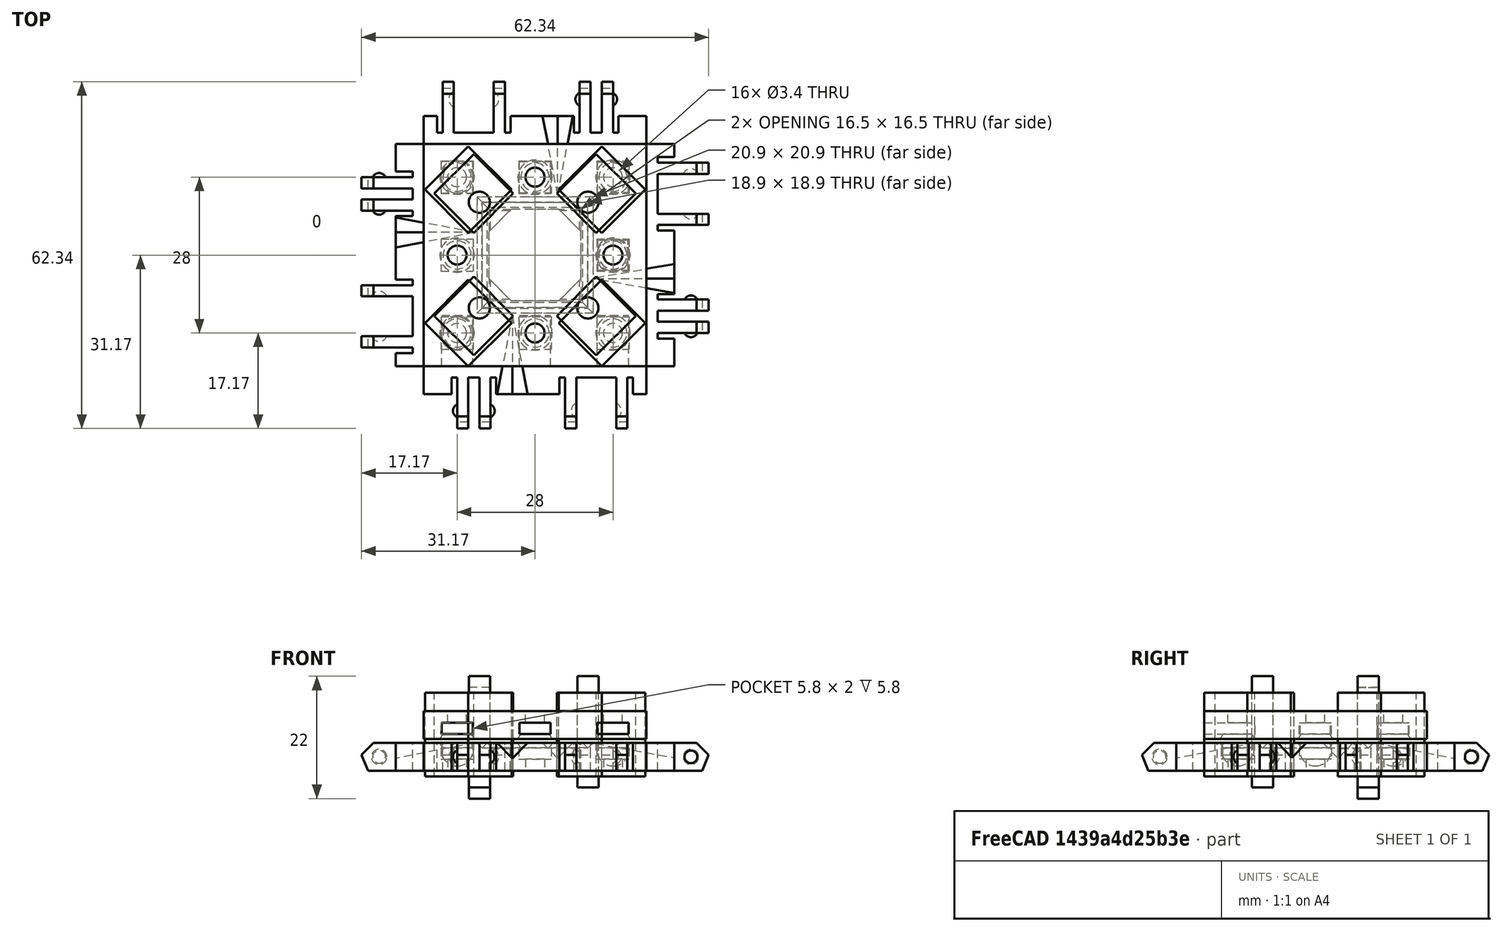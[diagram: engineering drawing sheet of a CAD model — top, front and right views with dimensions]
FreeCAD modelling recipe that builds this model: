
FCSTD DOCUMENT  (FreeCAD 0.17R13522 (Git))
Label: Robot Plates 0.3
License: All rights reserved
LicenseURL: http://en.wikipedia.org/wiki/All_rights_reserved
objects: Part::Box×147, Part::Sphere×51, Part::MultiFuse×48, Part::Cut×47, Part::Cylinder×24, Part::Chamfer×12, Part::Mirroring×2, Part::Fuse×2, App::DocumentObjectGroup×1
note: 333 computed .brp shape members not serialized (recipe doc carries the construction recipe); baked Part::Feature solids carry a one-line shape summary decoded from their .brp

FEATURE [Part::Box] Box  label="Cube"
  AttacherType = Attacher::AttachEngine3D
  Height = 5
  Length = 40
  Placement = pos=(0,0,-2) rot=(0,0,1;0rad)
  Width = 40
FEATURE [Part::Sphere] Sphere003  label="Mag Hole 3"
  Angle1 = -90
  Angle2 = 90
  Angle3 = 360
  AttacherType = Attacher::AttachEngine3D
  Placement = pos=(6,34,1.7) rot=(0,0,1;0rad)
  Radius = 2.85
FEATURE [Part::Sphere] Sphere005  label="Mag Hole 2"
  Angle1 = -90
  Angle2 = 90
  Angle3 = 360
  AttacherType = Attacher::AttachEngine3D
  Placement = pos=(34,20,1.7) rot=(0,0,1;0rad)
  Radius = 2.85
FEATURE [Part::Sphere] Sphere  label="Mag Hole"
  Angle1 = -90
  Angle2 = 90
  Angle3 = 360
  AttacherType = Attacher::AttachEngine3D
  Placement = pos=(6,6,1.7) rot=(0,0,1;0rad)
  Radius = 2.85
FEATURE [Part::MultiFuse] Fusion004
  Shapes = -> [Sphere,Sphere005,Sphere003]
FEATURE [Part::Cut] Cut003
  Base = -> Box
  Tool = -> Fusion004
FEATURE [Part::Box] Box001  label="Cube001"
  AttacherType = Attacher::AttachEngine3D
  Height = 7
  Length = 5
  Width = 40
FEATURE [Part::Box] Box002  label="Cube002"
  AttacherType = Attacher::AttachEngine3D
  Height = 7
  Length = 10
  Placement = pos=(-10,6,0) rot=(0,0,1;0rad)
  Width = 2
FEATURE [Part::Box] Box003  label="Cube003"
  AttacherType = Attacher::AttachEngine3D
  Height = 7
  Length = 10
  Placement = pos=(-10,10,0) rot=(0,0,1;0rad)
  Width = 2
FEATURE [Part::Box] Box004  label="Cube004"
  AttacherType = Attacher::AttachEngine3D
  Height = 7
  Length = 10
  Placement = pos=(-10,25.4,0) rot=(0,0,1;0rad)
  Width = 2
FEATURE [Part::Box] Box005  label="Cube005"
  AttacherType = Attacher::AttachEngine3D
  Height = 7
  Length = 10
  Placement = pos=(-10,34.6,0) rot=(0,0,1;0rad)
  Width = 2
FEATURE [Part::Sphere] Sphere008
  Angle1 = -90
  Angle2 = 90
  Angle3 = 360
  AttacherType = Attacher::AttachEngine3D
  Placement = pos=(-3,6.5,2.5) rot=(0,0,1;0rad)
  Radius = 1.25
FEATURE [Part::Box] Box006  label="Cube006"
  AttacherType = Attacher::AttachEngine3D
  Height = 10
  Length = 13
  Placement = pos=(-10.19,0,-1.19) rot=(0,-1,0;0.785398rad)
  Width = 40
FEATURE [Part::Sphere] Sphere009
  Angle1 = -90
  Angle2 = 90
  Angle3 = 360
  AttacherType = Attacher::AttachEngine3D
  Placement = pos=(-3,11.5,2.5) rot=(0,0,1;0rad)
  Radius = 1.25
FEATURE [Part::Sphere] Sphere010
  Angle1 = -90
  Angle2 = 90
  Angle3 = 360
  AttacherType = Attacher::AttachEngine3D
  Placement = pos=(-3,28,2.5) rot=(0,0,1;0rad)
  Radius = 1.5
FEATURE [Part::Sphere] Sphere011
  Angle1 = -90
  Angle2 = 90
  Angle3 = 360
  AttacherType = Attacher::AttachEngine3D
  Placement = pos=(-3,34,2.5) rot=(0,0,1;0rad)
  Radius = 1.5
FEATURE [Part::MultiFuse] Fusion
  Shapes = -> [Box001,Box002,Box003,Box004,Box005]
FEATURE [Part::Cut] Cut
  Base = -> Fusion
  Tool = -> Box006
FEATURE [Part::MultiFuse] Fusion001
  Shapes = -> [Sphere008,Sphere009,Cut]
FEATURE [Part::MultiFuse] Fusion002
  Shapes = -> [Sphere011,Sphere010]
FEATURE [Part::Cut] Cut001
  Base = -> Fusion001
  Tool = -> Fusion002
FEATURE [Part::Chamfer] Chamfer001
  Base = -> Cut001
  Edges = 4 edges r=4: [Edge31,Edge37,Edge43,Edge46]
FEATURE [Part::Box] Box007  label="Cube007"
  AttacherType = Attacher::AttachEngine3D
  Height = 7
  Length = 4
  Placement = pos=(-1,5,0) rot=(0,0,1;0rad)
  Width = 1
FEATURE [Part::Box] Box008  label="Cube008"
  AttacherType = Attacher::AttachEngine3D
  Height = 7
  Length = 4
  Placement = pos=(-1,8,0) rot=(0,0,1;0rad)
  Width = 2
FEATURE [Part::Box] Box009  label="Cube009"
  AttacherType = Attacher::AttachEngine3D
  Height = 7
  Length = 4
  Placement = pos=(-1,12,0) rot=(0,0,1;0rad)
  Width = 1
FEATURE [Part::Box] Box010  label="Cube010"
  AttacherType = Attacher::AttachEngine3D
  Height = 7
  Length = 4
  Placement = pos=(-1,24.4,0) rot=(0,0,1;0rad)
  Width = 1
FEATURE [Part::Box] Box011  label="Cube011"
  AttacherType = Attacher::AttachEngine3D
  Height = 7
  Length = 4
  Placement = pos=(-1,36.6,0) rot=(0,0,1;0rad)
  Width = 1
FEATURE [Part::Box] Box012  label="Cube012"
  AttacherType = Attacher::AttachEngine3D
  Height = 7
  Length = 4
  Placement = pos=(-1,27.4,0) rot=(0,0,1;0rad)
  Width = 7.2
FEATURE [Part::MultiFuse] Fusion003
  Shapes = -> [Box012,Box009,Box011,Box008,Box010,Box007]
FEATURE [Part::Cut] Cut002
  Base = -> Chamfer001
  Placement = pos=(-5,40,3) rot=(1,0,0;3.14159rad)
  Tool = -> Fusion003
FEATURE [Part::Box] Box013  label="Cube013"
  AttacherType = Attacher::AttachEngine3D
  Height = 10
  Length = 12
  Placement = pos=(-11,-2,-12) rot=(0,0,1;0rad)
  Width = 44
FEATURE [Part::Cut] Cut004
  Base = -> Cut002
  Tool = -> Box013
FEATURE [Part::Box] Box014  label="Cube014"
  AttacherType = Attacher::AttachEngine3D
  Height = 7
  Length = 10
  Placement = pos=(-10,34.6,0) rot=(0,0,1;0rad)
  Width = 2
FEATURE [Part::Box] Box015  label="Cube015"
  AttacherType = Attacher::AttachEngine3D
  Height = 7
  Length = 5
  Width = 40
FEATURE [Part::Box] Box016  label="Cube016"
  AttacherType = Attacher::AttachEngine3D
  Height = 7
  Length = 10
  Placement = pos=(-10,25.4,0) rot=(0,0,1;0rad)
  Width = 2
FEATURE [Part::Box] Box017  label="Cube017"
  AttacherType = Attacher::AttachEngine3D
  Height = 7
  Length = 10
  Placement = pos=(-10,10,0) rot=(0,0,1;0rad)
  Width = 2
FEATURE [Part::Box] Box018  label="Cube018"
  AttacherType = Attacher::AttachEngine3D
  Height = 7
  Length = 10
  Placement = pos=(-10,6,0) rot=(0,0,1;0rad)
  Width = 2
FEATURE [Part::Sphere] Sphere012
  Angle1 = -90
  Angle2 = 90
  Angle3 = 360
  AttacherType = Attacher::AttachEngine3D
  Placement = pos=(-3,6.5,2.5) rot=(0,0,1;0rad)
  Radius = 1.25
FEATURE [Part::Box] Box019  label="Cube019"
  AttacherType = Attacher::AttachEngine3D
  Height = 10
  Length = 13
  Placement = pos=(-10.19,0,-1.19) rot=(0,-1,0;0.785398rad)
  Width = 40
FEATURE [Part::Sphere] Sphere013
  Angle1 = -90
  Angle2 = 90
  Angle3 = 360
  AttacherType = Attacher::AttachEngine3D
  Placement = pos=(-3,11.5,2.5) rot=(0,0,1;0rad)
  Radius = 1.25
FEATURE [Part::Sphere] Sphere014
  Angle1 = -90
  Angle2 = 90
  Angle3 = 360
  AttacherType = Attacher::AttachEngine3D
  Placement = pos=(-3,28,2.5) rot=(0,0,1;0rad)
  Radius = 1.5
FEATURE [Part::Sphere] Sphere015
  Angle1 = -90
  Angle2 = 90
  Angle3 = 360
  AttacherType = Attacher::AttachEngine3D
  Placement = pos=(-3,34,2.5) rot=(0,0,1;0rad)
  Radius = 1.5
FEATURE [Part::MultiFuse] Fusion005
  Shapes = -> [Box015,Box018,Box017,Box016,Box014]
FEATURE [Part::Cut] Cut005
  Base = -> Fusion005
  Tool = -> Box019
FEATURE [Part::MultiFuse] Fusion006
  Shapes = -> [Sphere012,Sphere013,Cut005]
FEATURE [Part::MultiFuse] Fusion007
  Shapes = -> [Sphere015,Sphere014]
FEATURE [Part::Cut] Cut006
  Base = -> Fusion006
  Tool = -> Fusion007
FEATURE [Part::Chamfer] Chamfer002
  Base = -> Cut006
  Edges = 4 edges r=4: [Edge31,Edge37,Edge43,Edge46]
FEATURE [Part::Box] Box020  label="Cube020"
  AttacherType = Attacher::AttachEngine3D
  Height = 7
  Length = 4
  Placement = pos=(-1,5,0) rot=(0,0,1;0rad)
  Width = 1
FEATURE [Part::Box] Box021  label="Cube021"
  AttacherType = Attacher::AttachEngine3D
  Height = 7
  Length = 4
  Placement = pos=(-1,8,0) rot=(0,0,1;0rad)
  Width = 2
FEATURE [Part::Box] Box022  label="Cube022"
  AttacherType = Attacher::AttachEngine3D
  Height = 7
  Length = 4
  Placement = pos=(-1,12,0) rot=(0,0,1;0rad)
  Width = 1
FEATURE [Part::Box] Box023  label="Cube023"
  AttacherType = Attacher::AttachEngine3D
  Height = 7
  Length = 4
  Placement = pos=(-1,24.4,0) rot=(0,0,1;0rad)
  Width = 1
FEATURE [Part::Box] Box024  label="Cube024"
  AttacherType = Attacher::AttachEngine3D
  Height = 7
  Length = 4
  Placement = pos=(-1,36.6,0) rot=(0,0,1;0rad)
  Width = 1
FEATURE [Part::Box] Box025  label="Cube025"
  AttacherType = Attacher::AttachEngine3D
  Height = 7
  Length = 4
  Placement = pos=(-1,27.4,0) rot=(0,0,1;0rad)
  Width = 7.2
FEATURE [Part::MultiFuse] Fusion008
  Shapes = -> [Box025,Box022,Box024,Box021,Box023,Box020]
FEATURE [Part::Cut] Cut007
  Base = -> Chamfer002
  Placement = pos=(-5,40,3) rot=(1,0,0;3.14159rad)
  Tool = -> Fusion008
FEATURE [Part::Box] Box026  label="Cube026"
  AttacherType = Attacher::AttachEngine3D
  Height = 10
  Length = 12
  Placement = pos=(-11,-2,-12) rot=(0,0,1;0rad)
  Width = 44
FEATURE [Part::Cut] Cut008
  Base = -> Cut007
  Placement = pos=(40,0,0) rot=(0,0,1;1.5708rad)
  Tool = -> Box026
FEATURE [Part::Box] Box027  label="Cube027"
  AttacherType = Attacher::AttachEngine3D
  Height = 7
  Length = 4
  Placement = pos=(-1,12,0) rot=(0,0,1;0rad)
  Width = 1
FEATURE [Part::Box] Box028  label="Cube028"
  AttacherType = Attacher::AttachEngine3D
  Height = 10
  Length = 13
  Placement = pos=(-10.19,0,-1.19) rot=(0,-1,0;0.785398rad)
  Width = 40
FEATURE [Part::Box] Box029  label="Cube029"
  AttacherType = Attacher::AttachEngine3D
  Height = 7
  Length = 4
  Placement = pos=(-1,27.4,0) rot=(0,0,1;0rad)
  Width = 7.2
FEATURE [Part::Box] Box030  label="Cube030"
  AttacherType = Attacher::AttachEngine3D
  Height = 7
  Length = 4
  Placement = pos=(-1,5,0) rot=(0,0,1;0rad)
  Width = 1
FEATURE [Part::Box] Box031  label="Cube031"
  AttacherType = Attacher::AttachEngine3D
  Height = 7
  Length = 10
  Placement = pos=(-10,6,0) rot=(0,0,1;0rad)
  Width = 2
FEATURE [Part::Box] Box032  label="Cube032"
  AttacherType = Attacher::AttachEngine3D
  Height = 10
  Length = 12
  Placement = pos=(-11,-2,-12) rot=(0,0,1;0rad)
  Width = 44
FEATURE [Part::Sphere] Sphere016
  Angle1 = -90
  Angle2 = 90
  Angle3 = 360
  AttacherType = Attacher::AttachEngine3D
  Placement = pos=(-3,6.5,2.5) rot=(0,0,1;0rad)
  Radius = 1.25
FEATURE [Part::Box] Box033  label="Cube033"
  AttacherType = Attacher::AttachEngine3D
  Height = 7
  Length = 10
  Placement = pos=(-10,25.4,0) rot=(0,0,1;0rad)
  Width = 2
FEATURE [Part::Box] Box034  label="Cube034"
  AttacherType = Attacher::AttachEngine3D
  Height = 7
  Length = 10
  Placement = pos=(-10,10,0) rot=(0,0,1;0rad)
  Width = 2
FEATURE [Part::Sphere] Sphere017
  Angle1 = -90
  Angle2 = 90
  Angle3 = 360
  AttacherType = Attacher::AttachEngine3D
  Placement = pos=(-3,28,2.5) rot=(0,0,1;0rad)
  Radius = 1.5
FEATURE [Part::Sphere] Sphere018
  Angle1 = -90
  Angle2 = 90
  Angle3 = 360
  AttacherType = Attacher::AttachEngine3D
  Placement = pos=(-3,11.5,2.5) rot=(0,0,1;0rad)
  Radius = 1.25
FEATURE [Part::Box] Box035  label="Cube035"
  AttacherType = Attacher::AttachEngine3D
  Height = 7
  Length = 4
  Placement = pos=(-1,36.6,0) rot=(0,0,1;0rad)
  Width = 1
FEATURE [Part::Sphere] Sphere019
  Angle1 = -90
  Angle2 = 90
  Angle3 = 360
  AttacherType = Attacher::AttachEngine3D
  Placement = pos=(-3,34,2.5) rot=(0,0,1;0rad)
  Radius = 1.5
FEATURE [Part::MultiFuse] Fusion011
  Shapes = -> [Sphere019,Sphere017]
FEATURE [Part::Box] Box036  label="Cube036"
  AttacherType = Attacher::AttachEngine3D
  Height = 7
  Length = 4
  Placement = pos=(-1,8,0) rot=(0,0,1;0rad)
  Width = 2
FEATURE [Part::Box] Box037  label="Cube037"
  AttacherType = Attacher::AttachEngine3D
  Height = 7
  Length = 10
  Placement = pos=(-10,34.6,0) rot=(0,0,1;0rad)
  Width = 2
FEATURE [Part::Box] Box038  label="Cube038"
  AttacherType = Attacher::AttachEngine3D
  Height = 7
  Length = 4
  Placement = pos=(-1,24.4,0) rot=(0,0,1;0rad)
  Width = 1
FEATURE [Part::MultiFuse] Fusion009
  Shapes = -> [Box029,Box027,Box035,Box036,Box038,Box030]
FEATURE [Part::Box] Box039  label="Cube039"
  AttacherType = Attacher::AttachEngine3D
  Height = 7
  Length = 5
  Width = 40
FEATURE [Part::MultiFuse] Fusion012
  Shapes = -> [Box039,Box031,Box034,Box033,Box037]
FEATURE [Part::Cut] Cut011
  Base = -> Fusion012
  Tool = -> Box028
FEATURE [Part::MultiFuse] Fusion010
  Shapes = -> [Sphere016,Sphere018,Cut011]
FEATURE [Part::Cut] Cut012
  Base = -> Fusion010
  Tool = -> Fusion011
FEATURE [Part::Chamfer] Chamfer003
  Base = -> Cut012
  Edges = 4 edges r=4: [Edge31,Edge37,Edge43,Edge46]
FEATURE [Part::Cut] Cut010
  Base = -> Chamfer003
  Placement = pos=(-5,40,3) rot=(1,0,0;3.14159rad)
  Tool = -> Fusion009
FEATURE [Part::Cut] Cut009
  Base = -> Cut010
  Placement = pos=(40,40,0) rot=(0,0,1;3.14159rad)
  Tool = -> Box032
FEATURE [Part::Sphere] Sphere020
  Angle1 = -90
  Angle2 = 90
  Angle3 = 360
  AttacherType = Attacher::AttachEngine3D
  Placement = pos=(-3,11.5,2.5) rot=(0,0,1;0rad)
  Radius = 1.25
FEATURE [Part::Box] Box040  label="Cube040"
  AttacherType = Attacher::AttachEngine3D
  Height = 7
  Length = 10
  Placement = pos=(-10,6,0) rot=(0,0,1;0rad)
  Width = 2
FEATURE [Part::Box] Box041  label="Cube041"
  AttacherType = Attacher::AttachEngine3D
  Height = 7
  Length = 4
  Placement = pos=(-1,8,0) rot=(0,0,1;0rad)
  Width = 2
FEATURE [Part::Box] Box042  label="Cube042"
  AttacherType = Attacher::AttachEngine3D
  Height = 7
  Length = 10
  Placement = pos=(-10,10,0) rot=(0,0,1;0rad)
  Width = 2
FEATURE [Part::Box] Box043  label="Cube043"
  AttacherType = Attacher::AttachEngine3D
  Height = 10
  Length = 12
  Placement = pos=(-11,-2,-12) rot=(0,0,1;0rad)
  Width = 44
FEATURE [Part::Box] Box044  label="Cube044"
  AttacherType = Attacher::AttachEngine3D
  Height = 7
  Length = 4
  Placement = pos=(-1,5,0) rot=(0,0,1;0rad)
  Width = 1
FEATURE [Part::Sphere] Sphere021
  Angle1 = -90
  Angle2 = 90
  Angle3 = 360
  AttacherType = Attacher::AttachEngine3D
  Placement = pos=(-3,28,2.5) rot=(0,0,1;0rad)
  Radius = 1.5
FEATURE [Part::Sphere] Sphere022
  Angle1 = -90
  Angle2 = 90
  Angle3 = 360
  AttacherType = Attacher::AttachEngine3D
  Placement = pos=(-3,6.5,2.5) rot=(0,0,1;0rad)
  Radius = 1.25
FEATURE [Part::Sphere] Sphere023
  Angle1 = -90
  Angle2 = 90
  Angle3 = 360
  AttacherType = Attacher::AttachEngine3D
  Placement = pos=(-3,34,2.5) rot=(0,0,1;0rad)
  Radius = 1.5
FEATURE [Part::Box] Box045  label="Cube045"
  AttacherType = Attacher::AttachEngine3D
  Height = 7
  Length = 4
  Placement = pos=(-1,12,0) rot=(0,0,1;0rad)
  Width = 1
FEATURE [Part::Box] Box046  label="Cube046"
  AttacherType = Attacher::AttachEngine3D
  Height = 7
  Length = 5
  Width = 40
FEATURE [Part::Box] Box047  label="Cube047"
  AttacherType = Attacher::AttachEngine3D
  Height = 7
  Length = 4
  Placement = pos=(-1,36.6,0) rot=(0,0,1;0rad)
  Width = 1
FEATURE [Part::Box] Box048  label="Cube048"
  AttacherType = Attacher::AttachEngine3D
  Height = 7
  Length = 4
  Placement = pos=(-1,24.4,0) rot=(0,0,1;0rad)
  Width = 1
FEATURE [Part::Box] Box049  label="Cube049"
  AttacherType = Attacher::AttachEngine3D
  Height = 7
  Length = 10
  Placement = pos=(-10,25.4,0) rot=(0,0,1;0rad)
  Width = 2
FEATURE [Part::Box] Box050  label="Cube050"
  AttacherType = Attacher::AttachEngine3D
  Height = 10
  Length = 13
  Placement = pos=(-10.19,0,-1.19) rot=(0,-1,0;0.785398rad)
  Width = 40
FEATURE [Part::Box] Box051  label="Cube051"
  AttacherType = Attacher::AttachEngine3D
  Height = 7
  Length = 10
  Placement = pos=(-10,34.6,0) rot=(0,0,1;0rad)
  Width = 2
FEATURE [Part::MultiFuse] Fusion015
  Shapes = -> [Box046,Box040,Box042,Box049,Box051]
FEATURE [Part::Cut] Cut013
  Base = -> Fusion015
  Tool = -> Box050
FEATURE [Part::MultiFuse] Fusion013
  Shapes = -> [Sphere022,Sphere020,Cut013]
FEATURE [Part::MultiFuse] Fusion016
  Shapes = -> [Sphere023,Sphere021]
FEATURE [Part::Cut] Cut014
  Base = -> Fusion013
  Tool = -> Fusion016
FEATURE [Part::Chamfer] Chamfer004
  Base = -> Cut014
  Edges = 4 edges r=4: [Edge31,Edge37,Edge43,Edge46]
FEATURE [Part::Box] Box052  label="Cube052"
  AttacherType = Attacher::AttachEngine3D
  Height = 7
  Length = 4
  Placement = pos=(-1,27.4,0) rot=(0,0,1;0rad)
  Width = 7.2
FEATURE [Part::MultiFuse] Fusion014
  Shapes = -> [Box052,Box045,Box047,Box041,Box048,Box044]
FEATURE [Part::Cut] Cut016
  Base = -> Chamfer004
  Placement = pos=(-5,40,3) rot=(1,0,0;3.14159rad)
  Tool = -> Fusion014
FEATURE [Part::Cut] Cut015
  Base = -> Cut016
  Placement = pos=(0,40,0) rot=(0,0,-1;1.5708rad)
  Tool = -> Box043
FEATURE [Part::Box] Box054  label="Cube054"
  AttacherType = Attacher::AttachEngine3D
  Height = 15
  Length = 10
  Placement = pos=(9,2,-3) rot=(0,0,1;0.785398rad)
  Width = 10
FEATURE [Part::Box] Box055  label="Cube055"
  AttacherType = Attacher::AttachEngine3D
  Height = 15
  Length = 10
  Placement = pos=(31,24,-3) rot=(0,0,1;0.785398rad)
  Width = 10
FEATURE [Part::Box] Box056  label="Cube056"
  AttacherType = Attacher::AttachEngine3D
  Height = 15
  Length = 10
  Placement = pos=(31,2,-3) rot=(0,0,1;0.785398rad)
  Width = 10
FEATURE [Part::Box] Box057  label="Cube057"
  AttacherType = Attacher::AttachEngine3D
  Height = 15
  Length = 10
  Placement = pos=(9,24,-3) rot=(0,0,1;0.785398rad)
  Width = 10
FEATURE [Part::MultiFuse] Fusion017
  Shapes = -> [Box054,Box057,Box056,Box055]
FEATURE [Part::Box] Box058  label="Cube058"
  AttacherType = Attacher::AttachEngine3D
  Height = 5
  Length = 40
  Placement = pos=(0,0,3.7) rot=(0,0,1;0rad)
  Width = 40
FEATURE [Part::Box] Box059  label="Square Nut Hole 008"
  AttacherType = Attacher::AttachEngine3D
  Height = 2
  Length = 5.6
  Placement = pos=(17.2,31.2,4.6) rot=(0,0,1;0rad)
  Width = 5.6
FEATURE [Part::Box] Box060  label="Square Nut Hole 009"
  AttacherType = Attacher::AttachEngine3D
  Height = 2
  Length = 5.6
  Placement = pos=(17.2,-0.85,4.6) rot=(0,0,1;0rad)
  Width = 10
FEATURE [Part::Box] Box061  label="Square Nut Hole 010"
  AttacherType = Attacher::AttachEngine3D
  Height = 2
  Length = 5.6
  Placement = pos=(31.2,-0.85,4.6) rot=(0,0,1;0rad)
  Width = 10
FEATURE [Part::Box] Box062  label="Square Nut Hole 011"
  AttacherType = Attacher::AttachEngine3D
  Height = 2
  Length = 5.4
  Placement = pos=(31.3,17.3,4.6) rot=(0,0,1;0rad)
  Width = 5.4
FEATURE [Part::Box] Box063  label="Square Nut Hole 012"
  AttacherType = Attacher::AttachEngine3D
  Height = 2
  Length = 5.7
  Placement = pos=(3.15,31.15,4.6) rot=(0,0,1;0rad)
  Width = 5.7
FEATURE [Part::Box] Box064  label="Square Nut Hole 013"
  AttacherType = Attacher::AttachEngine3D
  Height = 2
  Length = 5.5
  Placement = pos=(31.25,31.25,4.6) rot=(0,0,1;0rad)
  Width = 5.5
FEATURE [Part::Box] Box065  label="Square Nut Hole 014"
  AttacherType = Attacher::AttachEngine3D
  Height = 2
  Length = 5.8
  Placement = pos=(3.1,17.1,4.6) rot=(0,0,1;0rad)
  Width = 5.8
FEATURE [Part::Box] Box066  label="Square Nut Hole 015"
  AttacherType = Attacher::AttachEngine3D
  Height = 2
  Length = 5.6
  Placement = pos=(3.2,-0.85,4.6) rot=(0,0,1;0rad)
  Width = 10
FEATURE [Part::Sphere] Sphere006  label="Nut Clearence1"
  Angle1 = -90
  Angle2 = 90
  Angle3 = 360
  AttacherType = Attacher::AttachEngine3D
  Placement = pos=(6,6,2.4) rot=(0,0,1;0rad)
  Radius = 3.35
FEATURE [Part::Sphere] Sphere024
  Angle1 = -90
  Angle2 = 90
  Angle3 = 360
  AttacherType = Attacher::AttachEngine3D
  Placement = pos=(6,34,2.4) rot=(0,0,1;0rad)
  Radius = 3.35
FEATURE [Part::Sphere] Sphere007
  Angle1 = -90
  Angle2 = 90
  Angle3 = 360
  AttacherType = Attacher::AttachEngine3D
  Placement = pos=(34,20,2.4) rot=(0,0,1;0rad)
  Radius = 3.35
FEATURE [Part::Sphere] Sphere001
  Angle1 = -90
  Angle2 = 90
  Angle3 = 360
  AttacherType = Attacher::AttachEngine3D
  Placement = pos=(34,6,2.4) rot=(0,0,1;0rad)
  Radius = 3.35
FEATURE [Part::Sphere] Sphere025
  Angle1 = -90
  Angle2 = 90
  Angle3 = 360
  AttacherType = Attacher::AttachEngine3D
  Placement = pos=(20,6,2.4) rot=(0,0,1;0rad)
  Radius = 3.35
FEATURE [Part::Sphere] Sphere026
  Angle1 = -90
  Angle2 = 90
  Angle3 = 360
  AttacherType = Attacher::AttachEngine3D
  Placement = pos=(20,34,2.4) rot=(0,0,1;0rad)
  Radius = 3.35
FEATURE [Part::Sphere] Sphere004
  Angle1 = -90
  Angle2 = 90
  Angle3 = 360
  AttacherType = Attacher::AttachEngine3D
  Placement = pos=(6,20,2.4) rot=(0,0,1;0rad)
  Radius = 3.35
FEATURE [Part::Sphere] Sphere002
  Angle1 = -90
  Angle2 = 90
  Angle3 = 360
  AttacherType = Attacher::AttachEngine3D
  Placement = pos=(34,34,2.4) rot=(0,0,1;0rad)
  Radius = 3.35
FEATURE [Part::Cylinder] Cylinder
  Angle = 360
  AttacherType = Attacher::AttachEngine3D
  Height = 10
  Placement = pos=(6,6,0) rot=(0,0,1;0rad)
  Radius = 1.7
FEATURE [Part::Cylinder] Cylinder002
  Angle = 360
  AttacherType = Attacher::AttachEngine3D
  Height = 10
  Placement = pos=(34,6,0) rot=(0,0,1;0rad)
  Radius = 1.7
FEATURE [Part::Cylinder] Cylinder001
  Angle = 360
  AttacherType = Attacher::AttachEngine3D
  Height = 10
  Placement = pos=(20,6,0) rot=(0,0,1;0rad)
  Radius = 1.7
FEATURE [Part::Cylinder] Cylinder003
  Angle = 360
  AttacherType = Attacher::AttachEngine3D
  Height = 10
  Placement = pos=(34,34,0) rot=(0,0,1;0rad)
  Radius = 1.7
FEATURE [Part::Cylinder] Cylinder004
  Angle = 360
  AttacherType = Attacher::AttachEngine3D
  Height = 10
  Placement = pos=(20,34,0) rot=(0,0,1;0rad)
  Radius = 1.7
FEATURE [Part::Cylinder] Cylinder005
  Angle = 360
  AttacherType = Attacher::AttachEngine3D
  Height = 10
  Placement = pos=(6,34,0) rot=(0,0,1;0rad)
  Radius = 1.7
FEATURE [Part::Cylinder] Cylinder006
  Angle = 360
  AttacherType = Attacher::AttachEngine3D
  Height = 10
  Placement = pos=(6,20,0) rot=(0,0,1;0rad)
  Radius = 1.7
FEATURE [Part::Cylinder] Cylinder007
  Angle = 360
  AttacherType = Attacher::AttachEngine3D
  Height = 10
  Placement = pos=(34,20,0) rot=(0,0,1;0rad)
  Radius = 1.7
FEATURE [Part::MultiFuse] Fusion018
  Shapes = -> [Cylinder,Cylinder004,Cylinder007,Cylinder005,Cylinder006,Cylinder001,Cylinder002,Cylinder003]
FEATURE [Part::MultiFuse] Fusion019
  Shapes = -> [Sphere007,Sphere024,Sphere006,Sphere025,Sphere001,Sphere026,Sphere004,Sphere002]
FEATURE [Part::MultiFuse] Fusion020
  Shapes = -> [Box061,Box065,Box062,Box063,Box064,Box066,Box059,Box060]
FEATURE [Part::Cut] Cut017
  Base = -> Box058
  Tool = -> Fusion020
FEATURE [Part::Cut] Cut019
  Base = -> Cut017
  Tool = -> Fusion019
FEATURE [Part::Cut] Cut018
  Base = -> Cut019
  Tool = -> Fusion018
FEATURE [Part::Cylinder] Cylinder008
  Angle = 360
  AttacherType = Attacher::AttachEngine3D
  Height = 20
  Placement = pos=(10,10.5,-5) rot=(0,0,1;0rad)
  Radius = 1.9
FEATURE [Part::Cylinder] Cylinder009
  Angle = 360
  AttacherType = Attacher::AttachEngine3D
  Height = 20
  Placement = pos=(29.5,10.5,-5) rot=(0,0,1;0rad)
  Radius = 1.9
FEATURE [Part::Cylinder] Cylinder010
  Angle = 360
  AttacherType = Attacher::AttachEngine3D
  Height = 20
  Placement = pos=(29.5,29.5,-5) rot=(0,0,1;0rad)
  Radius = 1.9
FEATURE [Part::Cylinder] Cylinder011
  Angle = 360
  AttacherType = Attacher::AttachEngine3D
  Height = 20
  Placement = pos=(10,29.5,-7) rot=(0,0,1;0rad)
  Radius = 1.9
FEATURE [Part::MultiFuse] Fusion021  label="M2 Screw holes"
  Shapes = -> [Cylinder008,Cylinder009,Cylinder011,Cylinder010]
FEATURE [Part::Box] Box067  label="Square Nut Hole 016"
  AttacherType = Attacher::AttachEngine3D
  Height = 2
  Length = 5.8
  Placement = pos=(31.1,17.1,4.6) rot=(0,0,1;0rad)
  Width = 5.8
FEATURE [Part::Box] Box068  label="Square Nut Hole 017"
  AttacherType = Attacher::AttachEngine3D
  Height = 2
  Length = 5.8
  Placement = pos=(17.1,3.1,4.6) rot=(0,0,1;0rad)
  Width = 5.8
FEATURE [Part::Box] Box069  label="Square Nut Hole 018"
  AttacherType = Attacher::AttachEngine3D
  Height = 2
  Length = 5.8
  Placement = pos=(31.1,3.1,4.6) rot=(0,0,1;0rad)
  Width = 5.8
FEATURE [Part::Box] Box070  label="Square Nut Hole 019"
  AttacherType = Attacher::AttachEngine3D
  Height = 2
  Length = 5.8
  Placement = pos=(3.1,3.1,4.6) rot=(0,0,1;0rad)
  Width = 5.8
FEATURE [Part::Box] Box071  label="Square Nut Hole 020"
  AttacherType = Attacher::AttachEngine3D
  Height = 2
  Length = 5.8
  Placement = pos=(3.1,31.1,4.6) rot=(0,0,1;0rad)
  Width = 5.8
FEATURE [Part::Box] Box072  label="Square Nut Hole 021"
  AttacherType = Attacher::AttachEngine3D
  Height = 2
  Length = 5.8
  Placement = pos=(17.1,31.1,4.6) rot=(0,0,1;0rad)
  Width = 5.8
FEATURE [Part::Box] Box073  label="Square Nut Hole 022"
  AttacherType = Attacher::AttachEngine3D
  Height = 2
  Length = 5.8
  Placement = pos=(31.1,31.1,4.6) rot=(0,0,1;0rad)
  Width = 5.8
FEATURE [Part::Box] Box074  label="Square Nut Hole 023"
  AttacherType = Attacher::AttachEngine3D
  Height = 2
  Length = 5.8
  Placement = pos=(3.1,17.1,4.6) rot=(0,0,1;0rad)
  Width = 5.8
FEATURE [Part::Cylinder] Cylinder012
  Angle = 360
  AttacherType = Attacher::AttachEngine3D
  Height = 10
  Placement = pos=(6,6,0) rot=(0,0,1;0rad)
  Radius = 1.7
FEATURE [Part::Cylinder] Cylinder013
  Angle = 360
  AttacherType = Attacher::AttachEngine3D
  Height = 10
  Placement = pos=(34,34,0) rot=(0,0,1;0rad)
  Radius = 1.7
FEATURE [Part::Cylinder] Cylinder014
  Angle = 360
  AttacherType = Attacher::AttachEngine3D
  Height = 10
  Placement = pos=(20,34,0) rot=(0,0,1;0rad)
  Radius = 1.7
FEATURE [Part::Cylinder] Cylinder015
  Angle = 360
  AttacherType = Attacher::AttachEngine3D
  Height = 10
  Placement = pos=(6,34,0) rot=(0,0,1;0rad)
  Radius = 1.7
FEATURE [Part::Cylinder] Cylinder016
  Angle = 360
  AttacherType = Attacher::AttachEngine3D
  Height = 10
  Placement = pos=(6,20,0) rot=(0,0,1;0rad)
  Radius = 1.7
FEATURE [Part::Cylinder] Cylinder017
  Angle = 360
  AttacherType = Attacher::AttachEngine3D
  Height = 10
  Placement = pos=(34,20,0) rot=(0,0,1;0rad)
  Radius = 1.7
FEATURE [Part::Cylinder] Cylinder018
  Angle = 360
  AttacherType = Attacher::AttachEngine3D
  Height = 10
  Placement = pos=(34,6,0) rot=(0,0,1;0rad)
  Radius = 1.7
FEATURE [Part::Cylinder] Cylinder019
  Angle = 360
  AttacherType = Attacher::AttachEngine3D
  Height = 10
  Placement = pos=(20,6,0) rot=(0,0,1;0rad)
  Radius = 1.7
FEATURE [Part::Box] Box075  label="Cube059"
  AttacherType = Attacher::AttachEngine3D
  Height = 5
  Length = 40
  Placement = pos=(0,0,-2) rot=(0,0,1;0rad)
  Width = 40
FEATURE [Part::Sphere] Sphere027
  Angle1 = -90
  Angle2 = 90
  Angle3 = 360
  AttacherType = Attacher::AttachEngine3D
  Placement = pos=(34,20,2.4) rot=(0,0,1;0rad)
  Radius = 3.35
FEATURE [Part::Sphere] Sphere028  label="Nut Clearence002"
  Angle1 = -90
  Angle2 = 90
  Angle3 = 360
  AttacherType = Attacher::AttachEngine3D
  Placement = pos=(6,6,2.4) rot=(0,0,1;0rad)
  Radius = 3.35
FEATURE [Part::Sphere] Sphere029
  Angle1 = -90
  Angle2 = 90
  Angle3 = 360
  AttacherType = Attacher::AttachEngine3D
  Placement = pos=(34,34,2.4) rot=(0,0,1;0rad)
  Radius = 3.35
FEATURE [Part::Sphere] Sphere030
  Angle1 = -90
  Angle2 = 90
  Angle3 = 360
  AttacherType = Attacher::AttachEngine3D
  Placement = pos=(34,6,2.4) rot=(0,0,1;0rad)
  Radius = 3.35
FEATURE [Part::Sphere] Sphere031
  Angle1 = -90
  Angle2 = 90
  Angle3 = 360
  AttacherType = Attacher::AttachEngine3D
  Placement = pos=(20,6,2.4) rot=(0,0,1;0rad)
  Radius = 3.35
FEATURE [Part::Sphere] Sphere032
  Angle1 = -90
  Angle2 = 90
  Angle3 = 360
  AttacherType = Attacher::AttachEngine3D
  Placement = pos=(6,34,2.4) rot=(0,0,1;0rad)
  Radius = 3.35
FEATURE [Part::Sphere] Sphere033
  Angle1 = -90
  Angle2 = 90
  Angle3 = 360
  AttacherType = Attacher::AttachEngine3D
  Placement = pos=(6,20,2.4) rot=(0,0,1;0rad)
  Radius = 3.35
FEATURE [Part::Sphere] Sphere034
  Angle1 = -90
  Angle2 = 90
  Angle3 = 360
  AttacherType = Attacher::AttachEngine3D
  Placement = pos=(20,34,2.4) rot=(0,0,1;0rad)
  Radius = 3.35
FEATURE [Part::Box] Box076  label="Cube060"
  AttacherType = Attacher::AttachEngine3D
  Height = 15
  Length = 16.5
  Placement = pos=(11.75,11.75,-3) rot=(0,0,1;0rad)
  Width = 16.5
FEATURE [Part::Box] Box077  label="Cube061"
  AttacherType = Attacher::AttachEngine3D
  Height = 15
  Length = 11
  Placement = pos=(8,24,-3) rot=(0,0,1;0.785398rad)
  Width = 11
FEATURE [Part::Box] Box078  label="Cube062"
  AttacherType = Attacher::AttachEngine3D
  Height = 15
  Length = 11
  Placement = pos=(8,0,-3) rot=(0,0,1;0.785398rad)
  Width = 11
FEATURE [Part::Box] Box079  label="Cube063"
  AttacherType = Attacher::AttachEngine3D
  Height = 15
  Length = 11
  Placement = pos=(32,0,-3) rot=(0,0,1;0.785398rad)
  Width = 11
FEATURE [Part::Box] Box080  label="Cube064"
  AttacherType = Attacher::AttachEngine3D
  Height = 15
  Length = 11
  Placement = pos=(32,24,-3) rot=(0,0,1;0.785398rad)
  Width = 11
FEATURE [Part::MultiFuse] Fusion022
  Shapes = -> [Box078,Box077,Box079,Box080]
FEATURE [Part::Cylinder] Cylinder020
  Angle = 360
  AttacherType = Attacher::AttachEngine3D
  Height = 20
  Placement = pos=(29.5,10.5,-5) rot=(0,0,1;0rad)
  Radius = 1.9
FEATURE [Part::Cylinder] Cylinder021
  Angle = 360
  AttacherType = Attacher::AttachEngine3D
  Height = 20
  Placement = pos=(10,29.5,-7) rot=(0,0,1;0rad)
  Radius = 1.9
FEATURE [Part::Cylinder] Cylinder022
  Angle = 360
  AttacherType = Attacher::AttachEngine3D
  Height = 20
  Placement = pos=(10,10.5,-5) rot=(0,0,1;0rad)
  Radius = 1.9
FEATURE [Part::Cylinder] Cylinder023
  Angle = 360
  AttacherType = Attacher::AttachEngine3D
  Height = 20
  Placement = pos=(29.5,29.5,-5) rot=(0,0,1;0rad)
  Radius = 1.9
FEATURE [Part::MultiFuse] Fusion023  label="M2 Screw holes001"
  Shapes = -> [Cylinder022,Cylinder020,Cylinder021,Cylinder023]
FEATURE [Part::MultiFuse] Fusion024  label="Square Nut Hole"
  Shapes = -> [Box067,Box073,Box071,Box069,Box068,Box070,Box072,Box074]
FEATURE [Part::MultiFuse] Fusion025  label="Square Nut Screw Holes"
  Shapes = -> [Cylinder012,Cylinder018,Cylinder016,Cylinder015,Cylinder014,Cylinder013,Cylinder017,Cylinder019]
FEATURE [Part::MultiFuse] Fusion026  label="Nut Chamfers"
  Shapes = -> [Sphere027,Sphere028,Sphere029,Sphere031,Sphere032,Sphere033,Sphere034,Sphere030]
FEATURE [App::DocumentObjectGroup] Group  label="Cubes"
  Group = -> [Fusion017,Fusion022]
FEATURE [Part::Box] Box082  label="Cube066"
  AttacherType = Attacher::AttachEngine3D
  Height = 10
  Length = 15
  Placement = pos=(30.8481,15.8,2.86019) rot=(0.974848,0.205904,-0.085288;0.803573rad)
  Width = 10
FEATURE [Part::Box] Box083  label="Cube067"
  AttacherType = Attacher::AttachEngine3D
  Height = 10
  Length = 21
  Placement = pos=(9.5,9.5,2.1) rot=(0,0,1;0rad)
  Width = 21
FEATURE [Part::Box] Box084  label="Cube068"
  AttacherType = Attacher::AttachEngine3D
  Height = 14
  Length = 17
  Placement = pos=(11.5,11.5,0) rot=(0,0,1;0rad)
  Width = 17
FEATURE [Part::Cut] Cut020
  Base = -> Box083
  Tool = -> Box084
FEATURE [Part::Chamfer] Chamfer007
  Base = -> Cut020
  Edges = 8 edges r=0.95: [Edge4,Edge5,Edge14,Edge16,Edge17,Edge18,Edge19,Edge20]
FEATURE [Part::Chamfer] Chamfer008
  Base = -> Box076
  Edges = 4 edges r=4: [Edge1,Edge3,Edge5,Edge7]
FEATURE [Part::Box] Box085  label="Cube069"
  AttacherType = Attacher::AttachEngine3D
  Height = 15
  Length = 16
  Placement = pos=(12,12,-13) rot=(0,0,1;0rad)
  Width = 16
FEATURE [Part::Box] Box086  label="Cube070"
  AttacherType = Attacher::AttachEngine3D
  Height = 10
  Length = 10
  Placement = pos=(17,32.0919,9.95) rot=(-0.225436,0.969773,-0.093378;0.807337rad)
  Width = 15
FEATURE [Part::Box] Box087  label="Cube071"
  AttacherType = Attacher::AttachEngine3D
  Height = 10
  Length = 10
  Placement = pos=(7.9081,17,9.95) rot=(-0.450607,0.280623,0.847469;1.65638rad)
  Width = 15
FEATURE [Part::Box] Box088  label="Cube072"
  AttacherType = Attacher::AttachEngine3D
  Height = 10
  Length = 10
  Placement = pos=(23,7.9081,9.95) rot=(-0.381178,-0.08861,0.920245;3.06822rad)
  Width = 15
FEATURE [Part::MultiFuse] Fusion027
  Shapes = -> [Box086,Box082,Box087,Box088]
FEATURE [Part::MultiFuse] Fusion028
  Shapes = -> [Cut015,Cut004,Cut008,Cut009]
FEATURE [Part::Box] Box089  label="Cube073"
  AttacherType = Attacher::AttachEngine3D
  Height = 10
  Length = 10
  Placement = pos=(17,32.0919,9.95) rot=(-0.225436,0.969773,-0.093378;0.807337rad)
  Width = 15
FEATURE [Part::Box] Box090  label="Cube074"
  AttacherType = Attacher::AttachEngine3D
  Height = 10
  Length = 15
  Placement = pos=(30.8481,15.8,2.86019) rot=(0.974848,0.205904,-0.085288;0.803573rad)
  Width = 10
FEATURE [Part::Box] Box091  label="Cube075"
  AttacherType = Attacher::AttachEngine3D
  Height = 10
  Length = 10
  Placement = pos=(7.9081,17,9.95) rot=(-0.450607,0.280623,0.847469;1.65638rad)
  Width = 15
FEATURE [Part::Box] Box092  label="Cube076"
  AttacherType = Attacher::AttachEngine3D
  Height = 10
  Length = 10
  Placement = pos=(23,7.9081,9.95) rot=(-0.381178,-0.08861,0.920245;3.06822rad)
  Width = 15
FEATURE [Part::Box] Box093  label="Cube077"
  AttacherType = Attacher::AttachEngine3D
  Height = 7
  Length = 5
  Width = 40
FEATURE [Part::Box] Box094  label="Cube078"
  AttacherType = Attacher::AttachEngine3D
  Height = 7
  Length = 10
  Placement = pos=(-10,6,0) rot=(0,0,1;0rad)
  Width = 2
FEATURE [Part::Box] Box095  label="Cube079"
  AttacherType = Attacher::AttachEngine3D
  Height = 7
  Length = 10
  Placement = pos=(-10,10,0) rot=(0,0,1;0rad)
  Width = 2
FEATURE [Part::Box] Box096  label="Cube080"
  AttacherType = Attacher::AttachEngine3D
  Height = 7
  Length = 10
  Placement = pos=(-10,25.4,0) rot=(0,0,1;0rad)
  Width = 2
FEATURE [Part::Box] Box097  label="Cube081"
  AttacherType = Attacher::AttachEngine3D
  Height = 7
  Length = 10
  Placement = pos=(-10,34.6,0) rot=(0,0,1;0rad)
  Width = 2
FEATURE [Part::Sphere] Sphere035
  Angle1 = -90
  Angle2 = 90
  Angle3 = 360
  AttacherType = Attacher::AttachEngine3D
  Placement = pos=(-3,6.5,2.5) rot=(0,0,1;0rad)
  Radius = 1.25
FEATURE [Part::Box] Box098  label="Cube082"
  AttacherType = Attacher::AttachEngine3D
  Height = 10
  Length = 13
  Placement = pos=(-10.19,0,-1.19) rot=(0,-1,0;0.785398rad)
  Width = 40
FEATURE [Part::Sphere] Sphere036
  Angle1 = -90
  Angle2 = 90
  Angle3 = 360
  AttacherType = Attacher::AttachEngine3D
  Placement = pos=(-3,11.5,2.5) rot=(0,0,1;0rad)
  Radius = 1.25
FEATURE [Part::Sphere] Sphere037
  Angle1 = -90
  Angle2 = 90
  Angle3 = 360
  AttacherType = Attacher::AttachEngine3D
  Placement = pos=(-3,28,2.5) rot=(0,0,1;0rad)
  Radius = 1.5
FEATURE [Part::Sphere] Sphere038
  Angle1 = -90
  Angle2 = 90
  Angle3 = 360
  AttacherType = Attacher::AttachEngine3D
  Placement = pos=(-3,34,2.5) rot=(0,0,1;0rad)
  Radius = 1.5
FEATURE [Part::MultiFuse] Fusion030
  Shapes = -> [Box093,Box094,Box095,Box096,Box097]
FEATURE [Part::Cut] Cut025
  Base = -> Fusion030
  Tool = -> Box098
FEATURE [Part::MultiFuse] Fusion031
  Shapes = -> [Sphere035,Sphere036,Cut025]
FEATURE [Part::MultiFuse] Fusion032
  Shapes = -> [Sphere038,Sphere037]
FEATURE [Part::Cut] Cut026
  Base = -> Fusion031
  Tool = -> Fusion032
FEATURE [Part::Chamfer] Chamfer009
  Base = -> Cut026
  Edges = 4 edges r=4: [Edge31,Edge37,Edge43,Edge46]
FEATURE [Part::Box] Box099  label="Cube083"
  AttacherType = Attacher::AttachEngine3D
  Height = 7
  Length = 4
  Placement = pos=(-1,5,0) rot=(0,0,1;0rad)
  Width = 1
FEATURE [Part::Box] Box100  label="Cube084"
  AttacherType = Attacher::AttachEngine3D
  Height = 7
  Length = 4
  Placement = pos=(-1,8,0) rot=(0,0,1;0rad)
  Width = 2
FEATURE [Part::Box] Box101  label="Cube085"
  AttacherType = Attacher::AttachEngine3D
  Height = 7
  Length = 4
  Placement = pos=(-1,12,0) rot=(0,0,1;0rad)
  Width = 1
FEATURE [Part::Box] Box102  label="Cube086"
  AttacherType = Attacher::AttachEngine3D
  Height = 7
  Length = 4
  Placement = pos=(-1,24.4,0) rot=(0,0,1;0rad)
  Width = 1
FEATURE [Part::Box] Box103  label="Cube087"
  AttacherType = Attacher::AttachEngine3D
  Height = 7
  Length = 4
  Placement = pos=(-1,36.6,0) rot=(0,0,1;0rad)
  Width = 1
FEATURE [Part::Box] Box104  label="Cube088"
  AttacherType = Attacher::AttachEngine3D
  Height = 7
  Length = 4
  Placement = pos=(-1,27.4,0) rot=(0,0,1;0rad)
  Width = 7.2
FEATURE [Part::MultiFuse] Fusion033
  Shapes = -> [Box104,Box101,Box103,Box100,Box102,Box099]
FEATURE [Part::Cut] Cut027
  Base = -> Chamfer009
  Placement = pos=(-5,40,3) rot=(1,0,0;3.14159rad)
  Tool = -> Fusion033
FEATURE [Part::Box] Box105  label="Cube089"
  AttacherType = Attacher::AttachEngine3D
  Height = 10
  Length = 12
  Placement = pos=(-11,-2,-12) rot=(0,0,1;0rad)
  Width = 44
FEATURE [Part::Cut] Cut028
  Base = -> Cut027
  Tool = -> Box105
FEATURE [Part::Box] Box106  label="Cube090"
  AttacherType = Attacher::AttachEngine3D
  Height = 7
  Length = 10
  Placement = pos=(-10,34.6,0) rot=(0,0,1;0rad)
  Width = 2
FEATURE [Part::Box] Box107  label="Cube091"
  AttacherType = Attacher::AttachEngine3D
  Height = 7
  Length = 5
  Width = 40
FEATURE [Part::Box] Box108  label="Cube092"
  AttacherType = Attacher::AttachEngine3D
  Height = 7
  Length = 10
  Placement = pos=(-10,25.4,0) rot=(0,0,1;0rad)
  Width = 2
FEATURE [Part::Box] Box109  label="Cube093"
  AttacherType = Attacher::AttachEngine3D
  Height = 7
  Length = 10
  Placement = pos=(-10,10,0) rot=(0,0,1;0rad)
  Width = 2
FEATURE [Part::Box] Box110  label="Cube094"
  AttacherType = Attacher::AttachEngine3D
  Height = 7
  Length = 10
  Placement = pos=(-10,6,0) rot=(0,0,1;0rad)
  Width = 2
FEATURE [Part::Sphere] Sphere039
  Angle1 = -90
  Angle2 = 90
  Angle3 = 360
  AttacherType = Attacher::AttachEngine3D
  Placement = pos=(-3,6.5,2.5) rot=(0,0,1;0rad)
  Radius = 1.25
FEATURE [Part::Box] Box111  label="Cube095"
  AttacherType = Attacher::AttachEngine3D
  Height = 10
  Length = 13
  Placement = pos=(-10.19,0,-1.19) rot=(0,-1,0;0.785398rad)
  Width = 40
FEATURE [Part::Sphere] Sphere040
  Angle1 = -90
  Angle2 = 90
  Angle3 = 360
  AttacherType = Attacher::AttachEngine3D
  Placement = pos=(-3,11.5,2.5) rot=(0,0,1;0rad)
  Radius = 1.25
FEATURE [Part::Sphere] Sphere041
  Angle1 = -90
  Angle2 = 90
  Angle3 = 360
  AttacherType = Attacher::AttachEngine3D
  Placement = pos=(-3,28,2.5) rot=(0,0,1;0rad)
  Radius = 1.5
FEATURE [Part::Sphere] Sphere042
  Angle1 = -90
  Angle2 = 90
  Angle3 = 360
  AttacherType = Attacher::AttachEngine3D
  Placement = pos=(-3,34,2.5) rot=(0,0,1;0rad)
  Radius = 1.5
FEATURE [Part::MultiFuse] Fusion034
  Shapes = -> [Box107,Box110,Box109,Box108,Box106]
FEATURE [Part::Cut] Cut029
  Base = -> Fusion034
  Tool = -> Box111
FEATURE [Part::MultiFuse] Fusion035
  Shapes = -> [Sphere039,Sphere040,Cut029]
FEATURE [Part::MultiFuse] Fusion036
  Shapes = -> [Sphere042,Sphere041]
FEATURE [Part::Cut] Cut030
  Base = -> Fusion035
  Tool = -> Fusion036
FEATURE [Part::Chamfer] Chamfer010
  Base = -> Cut030
  Edges = 4 edges r=4: [Edge31,Edge37,Edge43,Edge46]
FEATURE [Part::Box] Box112  label="Cube096"
  AttacherType = Attacher::AttachEngine3D
  Height = 7
  Length = 4
  Placement = pos=(-1,5,0) rot=(0,0,1;0rad)
  Width = 1
FEATURE [Part::Box] Box113  label="Cube097"
  AttacherType = Attacher::AttachEngine3D
  Height = 7
  Length = 4
  Placement = pos=(-1,8,0) rot=(0,0,1;0rad)
  Width = 2
FEATURE [Part::Box] Box114  label="Cube098"
  AttacherType = Attacher::AttachEngine3D
  Height = 7
  Length = 4
  Placement = pos=(-1,12,0) rot=(0,0,1;0rad)
  Width = 1
FEATURE [Part::Box] Box115  label="Cube099"
  AttacherType = Attacher::AttachEngine3D
  Height = 7
  Length = 4
  Placement = pos=(-1,24.4,0) rot=(0,0,1;0rad)
  Width = 1
FEATURE [Part::Box] Box116  label="Cube100"
  AttacherType = Attacher::AttachEngine3D
  Height = 7
  Length = 4
  Placement = pos=(-1,36.6,0) rot=(0,0,1;0rad)
  Width = 1
FEATURE [Part::Box] Box117  label="Cube101"
  AttacherType = Attacher::AttachEngine3D
  Height = 7
  Length = 4
  Placement = pos=(-1,27.4,0) rot=(0,0,1;0rad)
  Width = 7.2
FEATURE [Part::MultiFuse] Fusion037
  Shapes = -> [Box117,Box114,Box116,Box113,Box115,Box112]
FEATURE [Part::Cut] Cut031
  Base = -> Chamfer010
  Placement = pos=(-5,40,3) rot=(1,0,0;3.14159rad)
  Tool = -> Fusion037
FEATURE [Part::Box] Box118  label="Cube102"
  AttacherType = Attacher::AttachEngine3D
  Height = 10
  Length = 12
  Placement = pos=(-11,-2,-12) rot=(0,0,1;0rad)
  Width = 44
FEATURE [Part::Cut] Cut032
  Base = -> Cut031
  Placement = pos=(40,0,0) rot=(0,0,1;1.5708rad)
  Tool = -> Box118
FEATURE [Part::Box] Box119  label="Cube103"
  AttacherType = Attacher::AttachEngine3D
  Height = 7
  Length = 4
  Placement = pos=(-1,12,0) rot=(0,0,1;0rad)
  Width = 1
FEATURE [Part::Box] Box120  label="Cube104"
  AttacherType = Attacher::AttachEngine3D
  Height = 10
  Length = 13
  Placement = pos=(-10.19,0,-1.19) rot=(0,-1,0;0.785398rad)
  Width = 40
FEATURE [Part::Box] Box121  label="Cube105"
  AttacherType = Attacher::AttachEngine3D
  Height = 7
  Length = 4
  Placement = pos=(-1,27.4,0) rot=(0,0,1;0rad)
  Width = 7.2
FEATURE [Part::Box] Box122  label="Cube106"
  AttacherType = Attacher::AttachEngine3D
  Height = 7
  Length = 4
  Placement = pos=(-1,5,0) rot=(0,0,1;0rad)
  Width = 1
FEATURE [Part::Box] Box123  label="Cube107"
  AttacherType = Attacher::AttachEngine3D
  Height = 7
  Length = 10
  Placement = pos=(-10,6,0) rot=(0,0,1;0rad)
  Width = 2
FEATURE [Part::Box] Box124  label="Cube108"
  AttacherType = Attacher::AttachEngine3D
  Height = 10
  Length = 12
  Placement = pos=(-11,-2,-12) rot=(0,0,1;0rad)
  Width = 44
FEATURE [Part::Sphere] Sphere043
  Angle1 = -90
  Angle2 = 90
  Angle3 = 360
  AttacherType = Attacher::AttachEngine3D
  Placement = pos=(-3,6.5,2.5) rot=(0,0,1;0rad)
  Radius = 1.25
FEATURE [Part::Box] Box125  label="Cube109"
  AttacherType = Attacher::AttachEngine3D
  Height = 7
  Length = 10
  Placement = pos=(-10,25.4,0) rot=(0,0,1;0rad)
  Width = 2
FEATURE [Part::Box] Box126  label="Cube110"
  AttacherType = Attacher::AttachEngine3D
  Height = 7
  Length = 10
  Placement = pos=(-10,10,0) rot=(0,0,1;0rad)
  Width = 2
FEATURE [Part::Sphere] Sphere044
  Angle1 = -90
  Angle2 = 90
  Angle3 = 360
  AttacherType = Attacher::AttachEngine3D
  Placement = pos=(-3,28,2.5) rot=(0,0,1;0rad)
  Radius = 1.5
FEATURE [Part::Sphere] Sphere045
  Angle1 = -90
  Angle2 = 90
  Angle3 = 360
  AttacherType = Attacher::AttachEngine3D
  Placement = pos=(-3,11.5,2.5) rot=(0,0,1;0rad)
  Radius = 1.25
FEATURE [Part::Box] Box127  label="Cube111"
  AttacherType = Attacher::AttachEngine3D
  Height = 7
  Length = 4
  Placement = pos=(-1,36.6,0) rot=(0,0,1;0rad)
  Width = 1
FEATURE [Part::Sphere] Sphere046
  Angle1 = -90
  Angle2 = 90
  Angle3 = 360
  AttacherType = Attacher::AttachEngine3D
  Placement = pos=(-3,34,2.5) rot=(0,0,1;0rad)
  Radius = 1.5
FEATURE [Part::MultiFuse] Fusion040
  Shapes = -> [Sphere046,Sphere044]
FEATURE [Part::Box] Box128  label="Cube112"
  AttacherType = Attacher::AttachEngine3D
  Height = 7
  Length = 4
  Placement = pos=(-1,8,0) rot=(0,0,1;0rad)
  Width = 2
FEATURE [Part::Box] Box129  label="Cube113"
  AttacherType = Attacher::AttachEngine3D
  Height = 7
  Length = 10
  Placement = pos=(-10,34.6,0) rot=(0,0,1;0rad)
  Width = 2
FEATURE [Part::Box] Box130  label="Cube114"
  AttacherType = Attacher::AttachEngine3D
  Height = 7
  Length = 4
  Placement = pos=(-1,24.4,0) rot=(0,0,1;0rad)
  Width = 1
FEATURE [Part::MultiFuse] Fusion038
  Shapes = -> [Box121,Box119,Box127,Box128,Box130,Box122]
FEATURE [Part::Box] Box131  label="Cube115"
  AttacherType = Attacher::AttachEngine3D
  Height = 7
  Length = 5
  Width = 40
FEATURE [Part::MultiFuse] Fusion041
  Shapes = -> [Box131,Box123,Box126,Box125,Box129]
FEATURE [Part::Cut] Cut035
  Base = -> Fusion041
  Tool = -> Box120
FEATURE [Part::MultiFuse] Fusion039
  Shapes = -> [Sphere043,Sphere045,Cut035]
FEATURE [Part::Cut] Cut036
  Base = -> Fusion039
  Tool = -> Fusion040
FEATURE [Part::Chamfer] Chamfer011
  Base = -> Cut036
  Edges = 4 edges r=4: [Edge31,Edge37,Edge43,Edge46]
FEATURE [Part::Cut] Cut034
  Base = -> Chamfer011
  Placement = pos=(-5,40,3) rot=(1,0,0;3.14159rad)
  Tool = -> Fusion038
FEATURE [Part::Cut] Cut033
  Base = -> Cut034
  Placement = pos=(40,40,0) rot=(0,0,1;3.14159rad)
  Tool = -> Box124
FEATURE [Part::Sphere] Sphere047
  Angle1 = -90
  Angle2 = 90
  Angle3 = 360
  AttacherType = Attacher::AttachEngine3D
  Placement = pos=(-3,11.5,2.5) rot=(0,0,1;0rad)
  Radius = 1.25
FEATURE [Part::Box] Box132  label="Cube116"
  AttacherType = Attacher::AttachEngine3D
  Height = 7
  Length = 10
  Placement = pos=(-10,6,0) rot=(0,0,1;0rad)
  Width = 2
FEATURE [Part::Box] Box133  label="Cube117"
  AttacherType = Attacher::AttachEngine3D
  Height = 7
  Length = 4
  Placement = pos=(-1,8,0) rot=(0,0,1;0rad)
  Width = 2
FEATURE [Part::Box] Box134  label="Cube118"
  AttacherType = Attacher::AttachEngine3D
  Height = 7
  Length = 10
  Placement = pos=(-10,10,0) rot=(0,0,1;0rad)
  Width = 2
FEATURE [Part::Box] Box135  label="Cube119"
  AttacherType = Attacher::AttachEngine3D
  Height = 10
  Length = 12
  Placement = pos=(-11,-2,-12) rot=(0,0,1;0rad)
  Width = 44
FEATURE [Part::Box] Box136  label="Cube120"
  AttacherType = Attacher::AttachEngine3D
  Height = 7
  Length = 4
  Placement = pos=(-1,5,0) rot=(0,0,1;0rad)
  Width = 1
FEATURE [Part::Sphere] Sphere048
  Angle1 = -90
  Angle2 = 90
  Angle3 = 360
  AttacherType = Attacher::AttachEngine3D
  Placement = pos=(-3,28,2.5) rot=(0,0,1;0rad)
  Radius = 1.5
FEATURE [Part::Sphere] Sphere049
  Angle1 = -90
  Angle2 = 90
  Angle3 = 360
  AttacherType = Attacher::AttachEngine3D
  Placement = pos=(-3,6.5,2.5) rot=(0,0,1;0rad)
  Radius = 1.25
FEATURE [Part::Sphere] Sphere050
  Angle1 = -90
  Angle2 = 90
  Angle3 = 360
  AttacherType = Attacher::AttachEngine3D
  Placement = pos=(-3,34,2.5) rot=(0,0,1;0rad)
  Radius = 1.5
FEATURE [Part::Box] Box137  label="Cube121"
  AttacherType = Attacher::AttachEngine3D
  Height = 7
  Length = 4
  Placement = pos=(-1,12,0) rot=(0,0,1;0rad)
  Width = 1
FEATURE [Part::Box] Box138  label="Cube122"
  AttacherType = Attacher::AttachEngine3D
  Height = 7
  Length = 5
  Width = 40
FEATURE [Part::Box] Box139  label="Cube123"
  AttacherType = Attacher::AttachEngine3D
  Height = 7
  Length = 4
  Placement = pos=(-1,36.6,0) rot=(0,0,1;0rad)
  Width = 1
FEATURE [Part::Box] Box140  label="Cube124"
  AttacherType = Attacher::AttachEngine3D
  Height = 7
  Length = 4
  Placement = pos=(-1,24.4,0) rot=(0,0,1;0rad)
  Width = 1
FEATURE [Part::Box] Box141  label="Cube125"
  AttacherType = Attacher::AttachEngine3D
  Height = 7
  Length = 10
  Placement = pos=(-10,25.4,0) rot=(0,0,1;0rad)
  Width = 2
FEATURE [Part::Box] Box142  label="Cube126"
  AttacherType = Attacher::AttachEngine3D
  Height = 10
  Length = 13
  Placement = pos=(-10.19,0,-1.19) rot=(0,-1,0;0.785398rad)
  Width = 40
FEATURE [Part::Box] Box143  label="Cube127"
  AttacherType = Attacher::AttachEngine3D
  Height = 7
  Length = 10
  Placement = pos=(-10,34.6,0) rot=(0,0,1;0rad)
  Width = 2
FEATURE [Part::MultiFuse] Fusion044
  Shapes = -> [Box138,Box132,Box134,Box141,Box143]
FEATURE [Part::Cut] Cut037
  Base = -> Fusion044
  Tool = -> Box142
FEATURE [Part::MultiFuse] Fusion042
  Shapes = -> [Sphere049,Sphere047,Cut037]
FEATURE [Part::MultiFuse] Fusion045
  Shapes = -> [Sphere050,Sphere048]
FEATURE [Part::Cut] Cut038
  Base = -> Fusion042
  Tool = -> Fusion045
FEATURE [Part::Chamfer] Chamfer012
  Base = -> Cut038
  Edges = 4 edges r=4: [Edge31,Edge37,Edge43,Edge46]
FEATURE [Part::Box] Box144  label="Cube128"
  AttacherType = Attacher::AttachEngine3D
  Height = 7
  Length = 4
  Placement = pos=(-1,27.4,0) rot=(0,0,1;0rad)
  Width = 7.2
FEATURE [Part::MultiFuse] Fusion043
  Shapes = -> [Box144,Box137,Box139,Box133,Box140,Box136]
FEATURE [Part::Cut] Cut040
  Base = -> Chamfer012
  Placement = pos=(-5,40,3) rot=(1,0,0;3.14159rad)
  Tool = -> Fusion043
FEATURE [Part::Cut] Cut039
  Base = -> Cut040
  Placement = pos=(0,40,0) rot=(0,0,-1;1.5708rad)
  Tool = -> Box135
FEATURE [Part::MultiFuse] Fusion046
  Shapes = -> [Cut039,Cut028,Cut032,Cut033]
FEATURE [Part::MultiFuse] Fusion047
  Placement = pos=(0,40,6.7) rot=(1,0,0;3.14159rad)
  Shapes = -> [Fusion026,Fusion024,Fusion025]
FEATURE [Part::MultiFuse] Fusion048
  Shapes = -> [Box089,Box091,Box090,Box092]
FEATURE [Part::Box] Box145  label="Cube129"
  AttacherType = Attacher::AttachEngine3D
  Height = 15
  Length = 16
  Placement = pos=(12,12,-13) rot=(0,0,1;0rad)
  Width = 16
FEATURE [Part::Box] Box146  label="Cube130"
  AttacherType = Attacher::AttachEngine3D
  Height = 15
  Length = 16.5
  Placement = pos=(11.75,11.75,-3) rot=(0,0,1;0rad)
  Width = 16.5
FEATURE [Part::Chamfer] Chamfer013
  Base = -> Box146
  Edges = 4 edges r=4: [Edge1,Edge3,Edge5,Edge7]
FEATURE [Part::Box] Box147  label="Cube131"
  AttacherType = Attacher::AttachEngine3D
  Height = 10
  Length = 21
  Placement = pos=(9.5,9.5,2.1) rot=(0,0,1;0rad)
  Width = 21
FEATURE [Part::Box] Box148  label="Cube132"
  AttacherType = Attacher::AttachEngine3D
  Height = 14
  Length = 17
  Placement = pos=(11.5,11.5,0) rot=(0,0,1;0rad)
  Width = 17
FEATURE [Part::Cut] Cut043
  Base = -> Box147
  Tool = -> Box148
FEATURE [Part::Chamfer] Chamfer014
  Base = -> Cut043
  Edges = 8 edges r=0.95: [Edge4,Edge5,Edge14,Edge16,Edge17,Edge18,Edge19,Edge20]
FEATURE [Part::Cut] Cut047
  Base = -> Cut003
  Tool = -> Chamfer007
FEATURE [Part::Cut] Cut048
  Base = -> Cut047
  Tool = -> Chamfer008
FEATURE [Part::Cut] Cut049
  Base = -> Cut048
  Tool = -> Box085
FEATURE [Part::Mirroring] Part__Mirroring  label="Fusion028 (Mirror #1)"
  Base = (0,0,0)
  Normal = (0,0,1)
  Placement = pos=(0,0,1) rot=(0,0,1;0rad)
  Source = -> Fusion028
FEATURE [Part::Fuse] Fusion050
  Base = -> Cut049
  Tool = -> Part__Mirroring
FEATURE [Part::Cut] Cut050
  Base = -> Fusion050
  Tool = -> Fusion027
FEATURE [Part::Mirroring] Part__Mirroring001  label="Fusion046 (Mirror #2)"
  Base = (0,0,0)
  Normal = (0,0,1)
  Placement = pos=(0,0,1) rot=(0,0,1;0rad)
  Source = -> Fusion046
FEATURE [Part::Fuse] Fusion051
  Base = -> Box075
  Tool = -> Part__Mirroring001
FEATURE [Part::Cut] Cut051
  Base = -> Fusion051
  Tool = -> Fusion047
FEATURE [Part::Cut] Cut052
  Base = -> Cut051
  Tool = -> Fusion048
FEATURE [Part::Cut] Cut053
  Base = -> Cut052
  Tool = -> Chamfer014
FEATURE [Part::Cut] Cut054
  Base = -> Cut053
  Tool = -> Chamfer013
FEATURE [Part::Cut] Cut055
  Base = -> Cut054
  Tool = -> Box145
